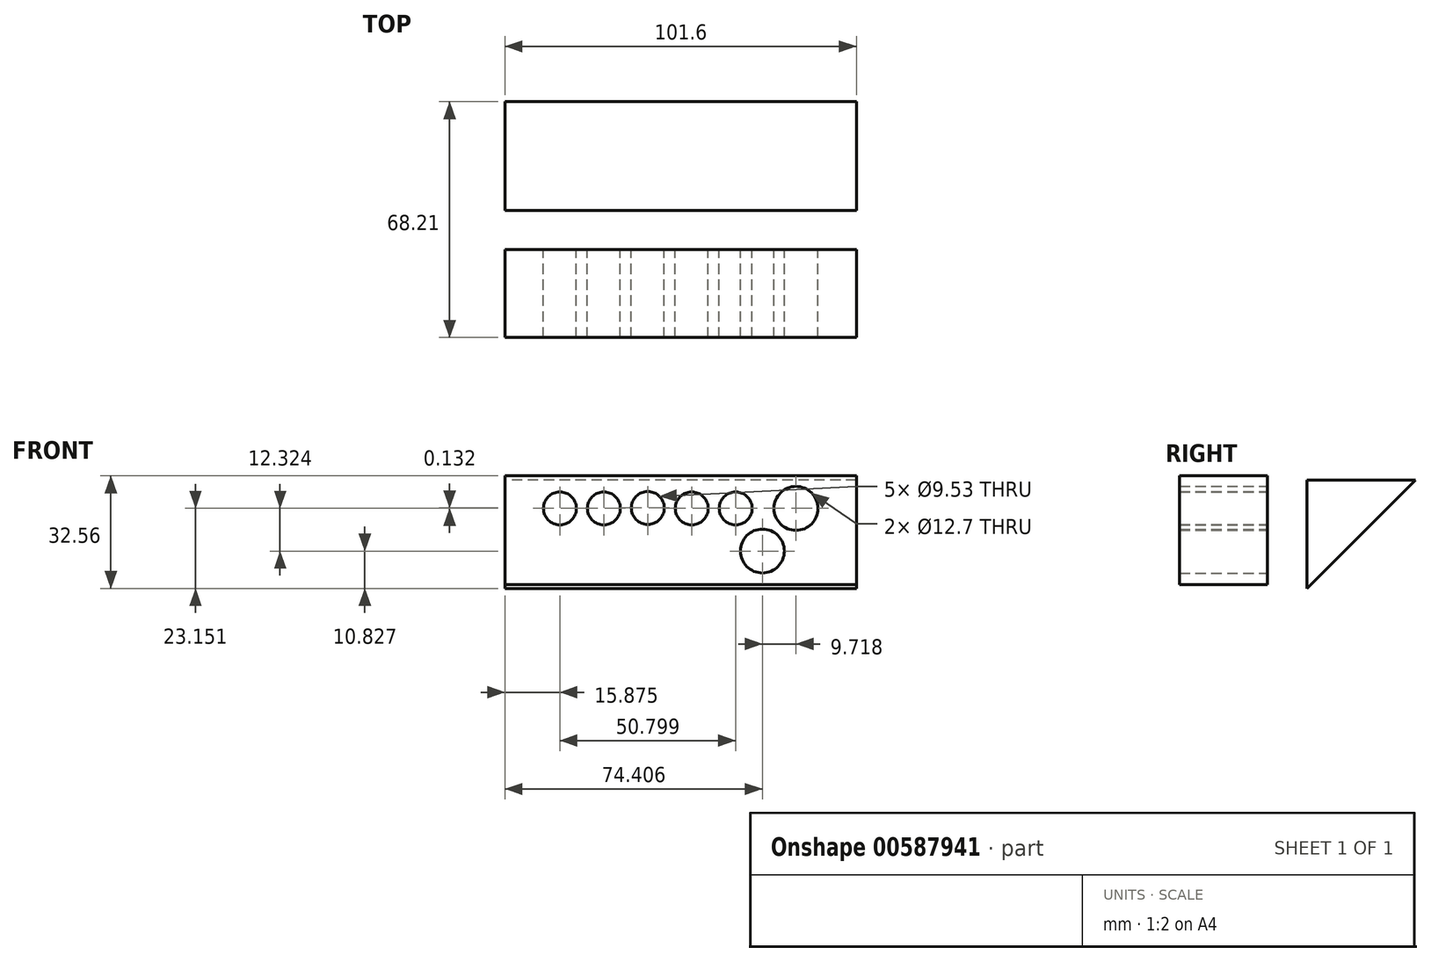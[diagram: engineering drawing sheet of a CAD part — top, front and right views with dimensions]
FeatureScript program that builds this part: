
annotation { "Feature Type Name" : "Feature", "Feature Type Description" : "" }
export const myFeature = defineFeature(function(context is Context, id is Id, definition is map)
    precondition{}
    {
        {
            var Q0;
            Q0=qCreatedBy(makeId("Front.planeOp"),FACE);
            var sketch = newSketch(context, id + "F0", { "sketchPlane" : qUnion([Q0])});
            skLineSegment(sketch, "E0.bottom", {"start": v(50.8, 19.05) * mm, "end": v(-50.8, 19.05) * mm});
            skLineSegment(sketch, "E0.left", {"start": v(50.8, 19.05) * mm, "end": v(50.8, -12.34) * mm});
            skLineSegment(sketch, "E0.right", {"start": v(-50.8, 19.05) * mm, "end": v(-50.8, -12.34) * mm});
            skPoint(sketch, "E0.middle", {"position": v(0, 0) * mm});
            skCircle(sketch, "E1", {"center": v(-34.93, 9.64) * mm, "radius": 4.76 * mm});
            skCircle(sketch, "E2", {"center": v(-22.23, 9.64) * mm, "radius": 4.76 * mm});
            skCircle(sketch, "E3", {"center": v(-9.53, 9.77) * mm, "radius": 4.76 * mm});
            skCircle(sketch, "E4", {"center": v(3.17, 9.64) * mm, "radius": 4.76 * mm});
            skCircle(sketch, "E5", {"center": v(15.87, 9.64) * mm, "radius": 4.76 * mm});
            skCircle(sketch, "E6", {"center": v(33.32, 9.64) * mm, "radius": 6.35 * mm});
            skCircle(sketch, "E7", {"center": v(23.6, -2.68) * mm, "radius": 6.35 * mm});
            skLineSegment(sketch, "E8", {"start": v(-50.8, -12.34) * mm, "end": v(50.8, -12.34) * mm});
            skSolve(sketch);
        }
        {
            var Q0;
            Q0=makeQuery(id+"F0.imprint","IMPRINT",FACE,{"disambiguationData":[TD([[makeQuery(id+"F0.imprint","IMPRINT",EDGE,{"derivedFrom":sQuery(id+"F0.wireOp",EDGE,"E0.bottom")}),1.0]])]});
            extrude(context, id + "F1", {"entities" : qUnion([Q0]), "depth" : 25.4 * mm, "offsetDistance" : 25.4 * mm});
        }
        {
            var Q0;
            Q0=qCreatedBy(makeId("Right.planeOp"),FACE);
            var sketch = newSketch(context, id + "F2", { "sketchPlane" : qUnion([Q0])});
            skLineSegment(sketch, "E9", {"start": v(11.42, 17.88) * mm, "end": v(11.42, -13.51) * mm});
            skLineSegment(sketch, "E10", {"start": v(11.42, -13.51) * mm, "end": v(24.93, 0) * mm});
            skLineSegment(sketch, "E11", {"start": v(24.93, 17.88) * mm, "end": v(11.42, 17.88) * mm});
            skLineSegment(sketch, "E12", {"start": v(24.93, 0) * mm, "end": v(42.81, 17.88) * mm});
            skLineSegment(sketch, "E13", {"start": v(42.81, 17.88) * mm, "end": v(24.93, 17.88) * mm});
            skSolve(sketch);
        }
        {
            var Q0;
            Q0 = qSketchRegion(id + "F2", true);
            extrude(context, id + "F3", {"entities" : qUnion([Q0]), "endBound" : BoundingType.SYMMETRIC, "depth" : 101.6 * mm, "offsetDistance" : 25.4 * mm});
        }
    });
